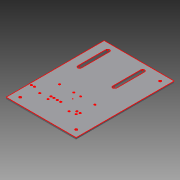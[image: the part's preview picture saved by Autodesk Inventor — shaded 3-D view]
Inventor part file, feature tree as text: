
AUTODESK INVENTOR PART (.ipt)
format: ipt  version: 2014 (Build 180170000, 170)  size: 292,864 bytes
history: native  units: in
note: dims shown in document units (in); Inventor stores cm internally (conversion verified against a paired STEP export)
features: hole x8, other x6, sketch x5, extrude x3
ambient origin geometry x8: Origin, YZ Plane, XZ Plane, XY Plane, X Axis, Y Axis, Z Axis, Center Point
bodies: Solid1 (feature_tree)
feature tree (22):
  extrude  "Extrusion1"  Depth=5.0in
  extrude  "Extrusion3"  Depth=2.5in
  hole  "Hole1"  [1 undecoded]
  extrude  "Extrusion2"  Depth=0.5in
  other  "battery buzzer/ SmartSensorPowered"
  other  "controller"
  other  "grizzly_bear"
  other  "koala_bear"
  other  "smartsensor"
  other  "team_flag"
  hole  "Hole2"  [1 undecoded]
  hole  "Hole3"  [1 undecoded]
  hole  "Hole4"  [1 undecoded]
  hole  "Hole5"  [1 undecoded]
  hole  "Hole6"  [1 undecoded]
  hole  "Hole7"  [1 undecoded]
  hole  "Hole8"  [1 undecoded]
  sketch  "Sketch14"  dims[d10=0.5in d11=0.5in d12=0.165in d13=0.75in d14=0.375in d15=0.25in d16=0.5635in d17=1.0in d18=0.8108in d19=0.27in d20=0.75in d21=0.5in d22=2.0in d23=0.25in d24=0.0in d25=1.0in d38=1.625in d39=0.25in d41=3.0in d46=3.0in d47=3.0in d58=1.255in d59=1.575in d64=1.1in d65=1.3in d78=1.6in d81=1.6in d83=0.13in d84=0.1in d85=0.1in d86=0.13in d89=0.13in d90=0.13in d95=0.1in d96=0.1in d99=0.1in d100=0.1in d108=0.13in d109=0.13in d110=0.13in d111=0.13in d112=0.2in d113=0.2in d114=0.2in d115=0.2in d116=0.2in d117=0.2in d118=0.2in d119=0.2in d120=0.13in d121=0.125in d122=0.11in d123=0.13in d124=0.11in d125=0.11in d126=0.13in d127=0.11in d128=0.125in d129=0.0938in d131=0.1in d137=0.15in d138=0.15in d139=0.15in d140=0.15in d141=0.15in d143=0.15in d144=0.1in d145=0.12in d146=0.12in d147=0.12in d148=0.12in d149=0.12in d150=0.12in d151=0.12in d152=0.755in d153=0.12in d154=0.125in d155=0.63in d156=1.25in d157=1.25in d187=0.3in d188=0.25in d194=0.3in d195=0.1in d197=0.094in d198=0.75in d199=0.375in d200=0.25in d201=0.5635in d202=1.0in d203=0.8108in d204=0.13in d205=0.75in d206=0.375in d207=0.25in d208=0.5635in d209=1.0in d210=0.8108in d211=0.13in d212=0.75in d213=0.375in d214=0.25in d215=0.5635in d216=1.0in d217=0.8108in d218=0.13in d219=0.75in d220=0.375in d221=0.25in d222=0.5635in d223=1.0in d224=0.8108in d225=0.0938in d226=0.75in d227=0.375in d228=0.25in d229=0.5635in d230=1.0in d231=0.8108in d232=0.12in d233=0.75in d234=0.375in d235=0.25in d236=0.5635in d237=1.0in d238=0.8108in d240=0.125in d241=0.0in d242=1.05in d248=1.85in d251=0.0938in d257=0.07in d258=0.08in d259=0.08in d266=0.1in d284=0.25in d286=0.3in d287=0.15in d288=0.165in d289=0.75in d290=0.375in d291=0.25in d292=0.5635in d293=1.0in d294=0.8108in d295=1.75in]
  sketch  "Sketch2"  dims[d0=5.0in d1=4.5in]
  sketch  "Sketch3"  dims[d2=2.5in d3=4.0in]
  sketch  "Sketch12"  dims[d4=0.125in d5=0.0in d7=4.0in]
  sketch  "Sketch13"  dims[d8=4.0in d9=0.5in]
note: 8 required parameter values undecoded (feature->parameter linkage not recoverable at this tier; creation-order binding heuristic only, values carry confidence <= 0.55)
